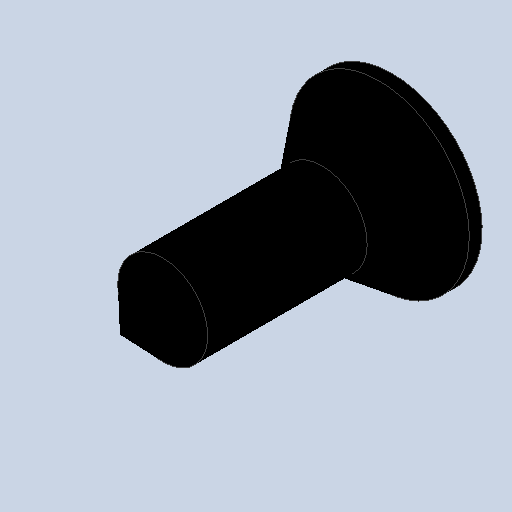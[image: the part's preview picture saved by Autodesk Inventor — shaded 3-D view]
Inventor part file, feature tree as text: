
AUTODESK INVENTOR PART (.ipt)
format: ipt  version: 2023 (Build 270158000, 158)  size: 134,656 bytes
history: native  units: mm
features: other x7, sketch x2, revolve x1, extrude x1
ambient origin geometry x8: Origin, YZ Plane, XZ Plane, XY Plane, X Axis, Y Axis, Z Axis, Center Point
bodies: Solid1 (feature_tree)
feature tree (11):
  revolve  "Revolution1"  [1 undecoded]
  extrude  "Extrusion1"  [1 undecoded]
  other  "CS_ANBAU_XY"
  other  "CS_ANBAU_YZ"
  other  "CS_ANBAU_ZX"
  other  "CS_ANBAU_X"
  other  "CS_ANBAU_Y"
  other  "CS_ANBAU_Z"
  other  "CS_ANBAU_Center"
  sketch  "Sketch_1"  dims[d0=360.0deg d1=2.0mm d2=0.0mm]
  sketch  "Sketch_3"  dims[d3=0.0mm]
note: 2 required parameter values undecoded (feature->parameter linkage not recoverable at this tier; creation-order binding heuristic only, values carry confidence <= 0.55)